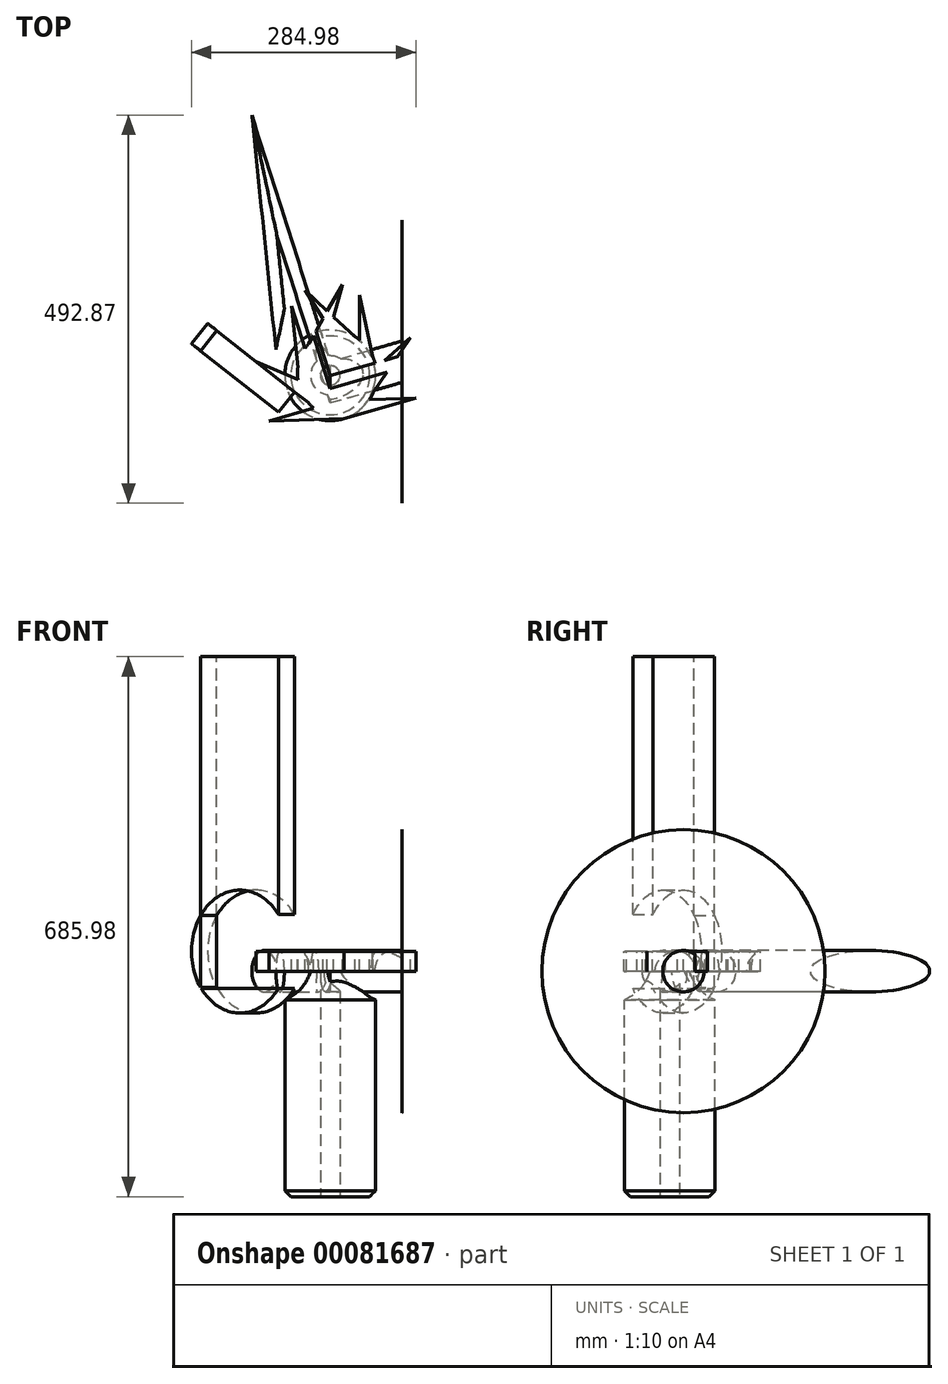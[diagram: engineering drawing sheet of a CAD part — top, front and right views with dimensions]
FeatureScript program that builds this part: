
annotation { "Feature Type Name" : "Feature", "Feature Type Description" : "" }
export const myFeature = defineFeature(function(context is Context, id is Id, definition is map)
    precondition{}
    {
        {
            var Q0;
            Q0=qCreatedBy(makeId("Front.planeOp"),FACE);
            var sketch = newSketch(context, id + "F0", { "sketchPlane" : qUnion([Q0])});
            skLineSegment(sketch, "E0", {"start": v(0, 125) * mm, "end": v(0, -125) * mm});
            skLineSegment(sketch, "E1", {"start": v(0, -125) * mm, "end": v(50, -125) * mm});
            skLineSegment(sketch, "E2", {"start": v(50, -125) * mm, "end": v(57.58, -117.43) * mm});
            skLineSegment(sketch, "E3", {"start": v(57.58, -117.43) * mm, "end": v(57.58, 125) * mm});
            skArc(sketch, "E4", {"start": v(23.06, 186.44) * mm, "mid": v(29.82, 149.82) * mm, "end": v(57.58, 125) * mm});
            skLineSegment(sketch, "E5", {"start": v(0, 125) * mm, "end": v(0, 186.44) * mm});
            skLineSegment(sketch, "E6", {"start": v(0, 186.44) * mm, "end": v(23.06, 186.44) * mm});
            skSolve(sketch);
        }
        {
            var Q0;
            Q0=makeQuery(id+"F0.imprint","IMPRINT",FACE,{"disambiguationData":[TD([[makeQuery(id+"F0.imprint","IMPRINT",EDGE,{"derivedFrom":sQuery(id+"F0.wireOp",EDGE,"E0")}),1.0]])]});
            var Q1;
            Q1=sQuery(id+"F0.wireOp",EDGE,"E0");
            revolve(context, id + "F1", {"entities" : qUnion([Q0]), "axis" : qUnion([Q1]), "revolveType" : RevolveType.FULL});
        }
        {
            var Q0;
            Q0=makeQuery(id+"F1.opRevolve","SWEPT_FACE",FACE,{"disambiguationData":[OSD([sQuery(id+"F0.wireOp",EDGE,"E1")])]});
            var sketch = newSketch(context, id + "F2", { "sketchPlane" : qUnion([Q0])});
            skCircle(sketch, "E7", {"center": v(0, 0) * mm, "radius": 12.43 * mm});
            skSolve(sketch);
        }
        {
            var Q0;
            Q0 = qSketchRegion(id + "F2", true);
            extrude(context, id + "F3", {"entities" : qUnion([Q0]), "operationType" : NewBodyOperationType.REMOVE, "oppositeDirection" : true, "depth" : 310 * mm});
        }
        {
            var Q0;
            Q0=makeQuery(id+"F1.opRevolve","SWEPT_FACE",FACE,{"disambiguationData":[OSD([sQuery(id+"F0.wireOp",EDGE,"E6")])]});
            var sketch = newSketch(context, id + "F4", { "sketchPlane" : qUnion([Q0])});
            skLineSegment(sketch, "E8", {"start": v(0, 57.58) * mm, "end": v(-32.24, 108.18) * mm});
            skLineSegment(sketch, "E9", {"start": v(-32.24, 108.18) * mm, "end": v(37.5, 43.68) * mm});
            skLineSegment(sketch, "E10", {"start": v(37.5, 43.68) * mm, "end": v(37.5, 101.7) * mm});
            skLineSegment(sketch, "E11", {"start": v(37.5, 101.7) * mm, "end": v(56.91, 8.7) * mm});
            skLineSegment(sketch, "E12", {"start": v(56.91, 8.7) * mm, "end": v(102.06, 48.22) * mm});
            skLineSegment(sketch, "E13", {"start": v(102.06, 48.22) * mm, "end": v(48.85, -30.48) * mm});
            skLineSegment(sketch, "E14", {"start": v(48.85, -30.48) * mm, "end": v(108.83, -28.81) * mm});
            skLineSegment(sketch, "E15", {"start": v(108.83, -28.81) * mm, "end": v(17.47, -54.86) * mm});
            skLineSegment(sketch, "E16", {"start": v(17.47, -54.86) * mm, "end": v(167, -43.8) * mm, "construction": true});
            skLineSegment(sketch, "E17", {"start": v(167, -43.8) * mm, "end": v(86.9, -94.86) * mm, "construction": true});
            skLineSegment(sketch, "E18", {"start": v(86.9, -94.86) * mm, "end": v(215.75, -96.7) * mm, "construction": true});
            skLineSegment(sketch, "E19", {"start": v(215.75, -96.7) * mm, "end": v(167, -178.24) * mm, "construction": true});
            skLineSegment(sketch, "E20", {"start": v(167, -178.24) * mm, "end": v(274.56, -132.35) * mm, "construction": true});
            skLineSegment(sketch, "E21", {"start": v(274.56, -132.35) * mm, "end": v(233.97, -218.24) * mm, "construction": true});
            skArc(sketch, "E22", {"start": v(17.47, -54.86) * mm, "mid": v(58.4, 9.07) * mm, "end": v(0, 57.58) * mm});
            skLineSegment(sketch, "E23", {"start": v(-31.34, 259.3) * mm, "end": v(50.31, -266.28) * mm, "construction": true});
            skLineSegment(sketch, "E24.MirrorCS", {"start": v(15.37, 115.57) * mm, "end": v(-31.53, 32.96) * mm});
            skLineSegment(sketch, "E25.MirrorCS", {"start": v(0, 57.58) * mm, "end": v(15.37, 115.57) * mm});
            skLineSegment(sketch, "E26.MirrorCS", {"start": v(-19.83, -41.15) * mm, "end": v(-77.49, -57.76) * mm});
            skLineSegment(sketch, "E27.MirrorCS", {"start": v(-94.41, 17.7) * mm, "end": v(-19.83, -41.15) * mm});
            skLineSegment(sketch, "E28.MirrorCS", {"start": v(-204, -206.69) * mm, "end": v(-139.27, -276.22) * mm, "construction": true});
            skArc(sketch, "E29.MirrorCS", {"start": v(17.47, -54.86) * mm, "mid": v(-40.93, -6.36) * mm, "end": v(0, 57.58) * mm});
            skLineSegment(sketch, "E30.MirrorCS", {"start": v(17.47, -54.86) * mm, "end": v(-128.38, -89.69) * mm, "construction": true});
            skLineSegment(sketch, "E31.MirrorCS", {"start": v(-39.4, -6.26) * mm, "end": v(-94.41, 17.7) * mm});
            skLineSegment(sketch, "E32.MirrorCS", {"start": v(-31.53, 32.96) * mm, "end": v(-49.13, 88.24) * mm});
            skLineSegment(sketch, "E33.MirrorCS", {"start": v(-87.6, -217.8) * mm, "end": v(-204, -206.69) * mm, "construction": true});
            skLineSegment(sketch, "E34.MirrorCS", {"start": v(-36.55, -114.04) * mm, "end": v(-158.78, -154.88) * mm, "construction": true});
            skLineSegment(sketch, "E35.MirrorCS", {"start": v(-158.78, -154.88) * mm, "end": v(-87.6, -217.8) * mm, "construction": true});
            skLineSegment(sketch, "E36.MirrorCS", {"start": v(-77.49, -57.76) * mm, "end": v(17.47, -54.86) * mm});
            skLineSegment(sketch, "E37.MirrorCS", {"start": v(-128.38, -89.69) * mm, "end": v(-36.55, -114.04) * mm, "construction": true});
            skLineSegment(sketch, "E38.MirrorCS", {"start": v(-49.13, 88.24) * mm, "end": v(-39.4, -6.26) * mm});
            skSolve(sketch);
        }
        {
            var Q0;
            Q0 = qSketchRegion(id + "F4", true);
            extrude(context, id + "F5", {"entities" : qUnion([Q0]), "operationType" : NewBodyOperationType.ADD, "oppositeDirection" : true, "depth" : 25 * mm});
        }
        {
            var Q0;
            Q0=qCreatedBy(makeId("Right.planeOp"),FACE);
            var sketch = newSketch(context, id + "F6", { "sketchPlane" : qUnion([Q0])});
            skCircle(sketch, "E39", {"center": v(-8.56, 161.44) * mm, "radius": 26.26 * mm});
            skSolve(sketch);
        }
        {
            var Q0;
            Q0 = qSketchRegion(id + "F6", true);
            var Q1;
            Q1=makeQuery(id+"F5.opExtrude","CAP_EDGE",EDGE,{"disambiguationData":[OSD([sQuery(id+"F4.wireOp",EDGE,"E32.MirrorCS")])],"isStart":true});
            var Q2;
            Q2=makeQuery(id+"F5.opExtrude","CAP_EDGE",EDGE,{"disambiguationData":[OSD([sQuery(id+"F4.wireOp",EDGE,"E38.MirrorCS")])],"isStart":true});
            sweep(context, id + "F7", {"operationType" : NewBodyOperationType.ADD, "profiles" : qUnion([Q0]), "path" : qUnion([Q1, Q2])});
        }
        {
            var Q0;
            Q0 = qSketchRegion(id + "F6", true);
            var Q1;
            Q1=makeQuery(id+"F5.opExtrude","CAP_EDGE",EDGE,{"disambiguationData":[OSD([sQuery(id+"F4.wireOp",EDGE,"E15")])],"isStart":true});
            sweep(context, id + "F8", {"operationType" : NewBodyOperationType.ADD, "profiles" : qUnion([Q0]), "path" : qUnion([Q1])});
        }
        {
            var Q0;
            Q0=makeQuery(id+"F8.opSweep","CAP_FACE",FACE,{"disambiguationData":[OSD([sQuery(id+"F4.wireOp",EDGE,"E14"),sQuery(id+"F4.wireOp",EDGE,"E15"),sQuery(id+"F6.wireOp",EDGE,"E39")])],"isStart":false});
            var sketch = newSketch(context, id + "F9", { "sketchPlane" : qUnion([Q0])});
            skCircle(sketch, "E40", {"center": v(17.5, 161.44) * mm, "radius": 179.81 * mm});
            skSolve(sketch);
        }
        {
            var Q0;
            Q0=makeQuery(id+"F9.imprint","IMPRINT",FACE,{"disambiguationData":[TD([[makeQuery(id+"F9.imprint","IMPRINT",EDGE,{"derivedFrom":sQuery(id+"F9.wireOp",EDGE,"E40")}),1.0]])]});
            extrude(context, id + "F10", {"entities" : qUnion([Q0]), "oppositeDirection" : true, "depth" : .1 * mm});
        }
        {
            var Q0;
            Q0=makeQuery(id+"F5.opExtrude","SWEPT_FACE",FACE,{"disambiguationData":[OSD([sQuery(id+"F4.wireOp",EDGE,"E27.MirrorCS")])]});
            var sketch = newSketch(context, id + "F11", { "sketchPlane" : qUnion([Q0])});
            skCircle(sketch, "E41", {"center": v(-85.08, 186.44) * mm, "radius": 78.08 * mm});
            skLineSegment(sketch, "E42.bottom", {"start": v(-22.69, 139.5) * mm, "end": v(-148.48, 139.5) * mm});
            skLineSegment(sketch, "E42.top", {"start": v(-22.69, 560.98) * mm, "end": v(-148.48, 560.98) * mm});
            skLineSegment(sketch, "E42.left", {"start": v(-22.69, 139.5) * mm, "end": v(-22.69, 560.98) * mm});
            skLineSegment(sketch, "E42.right", {"start": v(-148.48, 139.5) * mm, "end": v(-148.48, 560.98) * mm});
            skSolve(sketch);
        }
        {
            var Q0;
            {var subQ5=sQuery(id+"F11.wireOp",EDGE,"E42.top");Q0=makeQuery(id+"F11.imprint","IMPRINT",FACE,{"disambiguationData":[TD([[makeQuery(id+"F11.imprint","IMPRINT",EDGE,{"derivedFrom":subQ5}),1.0]])]});}
            var Q1;
            {var subQ0=sQuery(id+"F11.wireOp",EDGE,"E42.right");var subQ1=sQuery(id+"F11.wireOp",EDGE,"E41");var subQ2=makeQuery(id+"F11.imprint","INTERSECT",VERTEX,{"disambiguationData":[OD(0.0)],"derivedFrom":[subQ1,subQ0]});Q1=makeQuery(id+"F11.imprint","IMPRINT",FACE,{"disambiguationData":[TD([[makeQuery(id+"F11.imprint","IMPRINT",EDGE,{"disambiguationData":[TD([[subQ2,-1.0]])],"derivedFrom":subQ1}),1.0]])]});}
            var Q2;
            {var subQ0=sQuery(id+"F11.wireOp",EDGE,"E42.bottom");var subQ1=sQuery(id+"F11.wireOp",EDGE,"E41");var subQ3=makeQuery(id+"F11.imprint","INTERSECT",VERTEX,{"derivedFrom":[subQ1,subQ0]});Q2=makeQuery(id+"F11.imprint","IMPRINT",FACE,{"disambiguationData":[TD([[makeQuery(id+"F11.imprint","IMPRINT",EDGE,{"disambiguationData":[TD([[subQ3,-1.0]])],"derivedFrom":subQ1}),1.0]])]});}
            extrude(context, id + "F12", {"entities" : qUnion([Q0, Q1, Q2]), "depth" : 33 * mm});
        }
    });
